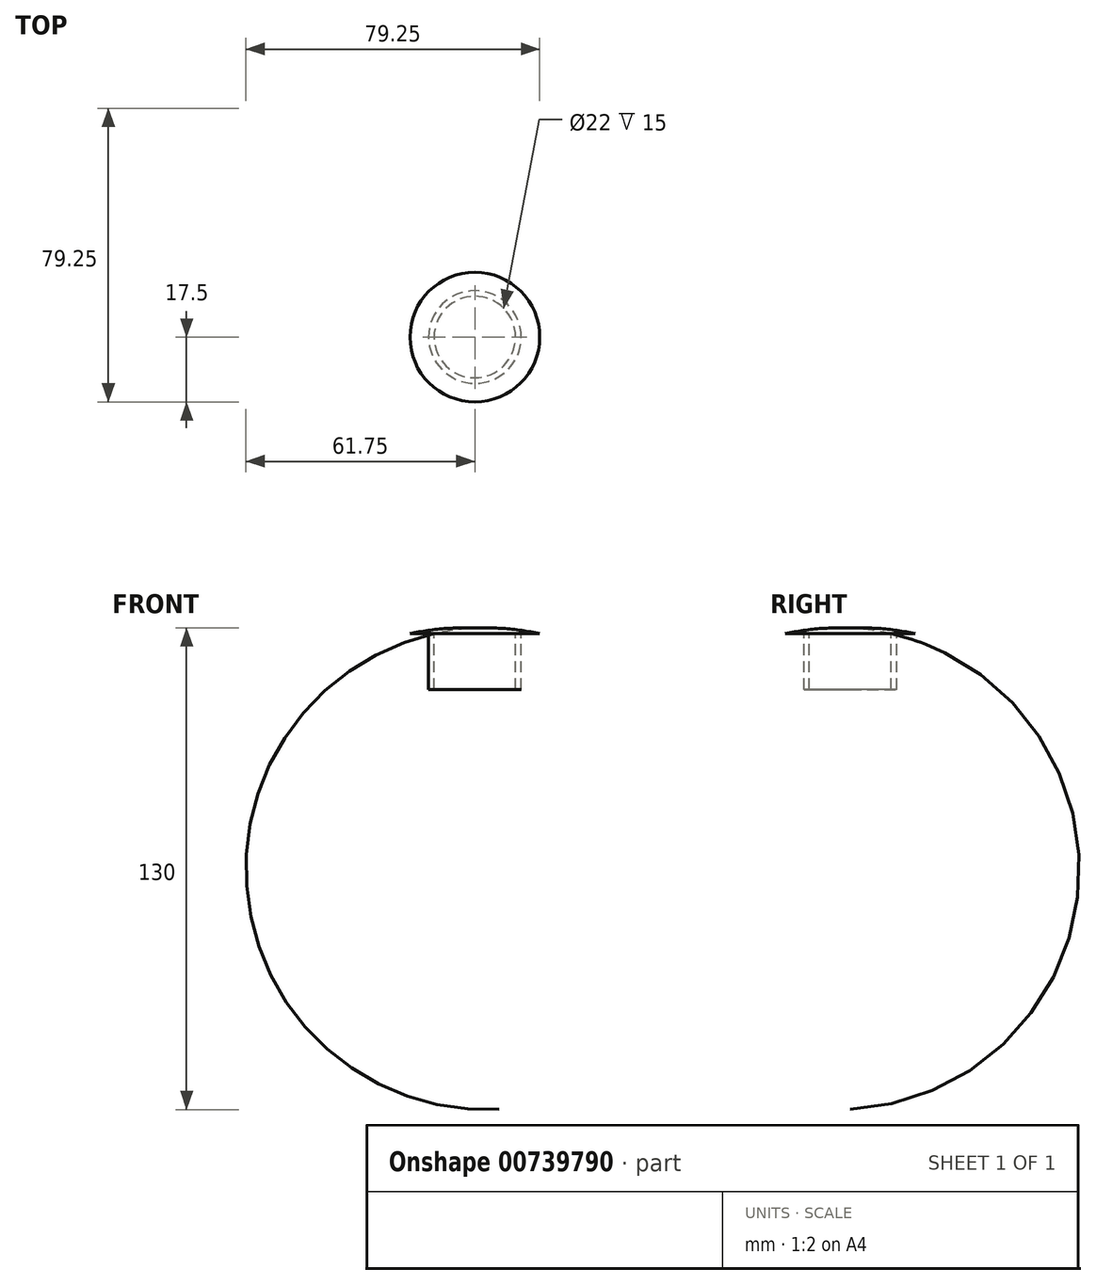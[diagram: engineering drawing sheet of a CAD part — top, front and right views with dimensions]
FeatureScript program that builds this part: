
annotation { "Feature Type Name" : "Feature", "Feature Type Description" : "" }
export const myFeature = defineFeature(function(context is Context, id is Id, definition is map)
    precondition{}
    {
        {
            var Q0;
            Q0=qCreatedBy(makeId("Front.planeOp"),FACE);
            var sketch = newSketch(context, id + "F0", { "sketchPlane" : qUnion([Q0])});
            skLineSegment(sketch, "E0", {"start": v(0, 15) * mm, "end": v(12.5, 15) * mm});
            skLineSegment(sketch, "E1", {"start": v(12.5, 15) * mm, "end": v(12.5, 0) * mm});
            skArc(sketch, "E2", {"start": v(17.5, 15) * mm, "mid": v(8.8, 16.34) * mm, "end": v(0, 16.5) * mm});
            skLineSegment(sketch, "E3", {"start": v(0, 16.5) * mm, "end": v(0, 15) * mm});
            skLineSegment(sketch, "E4", {"start": v(0, 15) * mm, "end": v(17.5, 15) * mm});
            skLineSegment(sketch, "E5", {"start": v(11, 15) * mm, "end": v(11, 0) * mm});
            skLineSegment(sketch, "E6", {"start": v(0, 8.27) * mm, "end": v(11, 8.27) * mm, "construction": true});
            skLineSegment(sketch, "E7", {"start": v(11, 0) * mm, "end": v(12.5, 0) * mm});
            skLineSegment(sketch, "E8", {"start": v(11, 15) * mm, "end": v(12.5, 15) * mm});
            skSolve(sketch);
        }
        {
            var Q0;
            {var subQ2=sQuery(id+"F0.wireOp",EDGE,"E2");Q0=makeQuery(id+"F0.imprint","IMPRINT",FACE,{"disambiguationData":[TD([[makeQuery(id+"F0.imprint","IMPRINT",EDGE,{"derivedFrom":subQ2}),1.0]])]});}
            var Q1;
            Q1=makeQuery(id+"F0.imprint","IMPRINT",FACE,{"disambiguationData":[TD([[makeQuery(id+"F0.imprint","IMPRINT",EDGE,{"derivedFrom":sQuery(id+"F0.wireOp",EDGE,"E1")}),-1.0]])]});
            var Q2;
            Q2=sQuery(id+"F0.wireOp",EDGE,"E3");
            revolve(context, id + "F1", {"surfaceOperationType" : NewSurfaceOperationType.NEW, "entities" : qUnion([Q0, Q1]), "axis" : qUnion([Q2]), "revolveType" : RevolveType.FULL});
        }
    });
